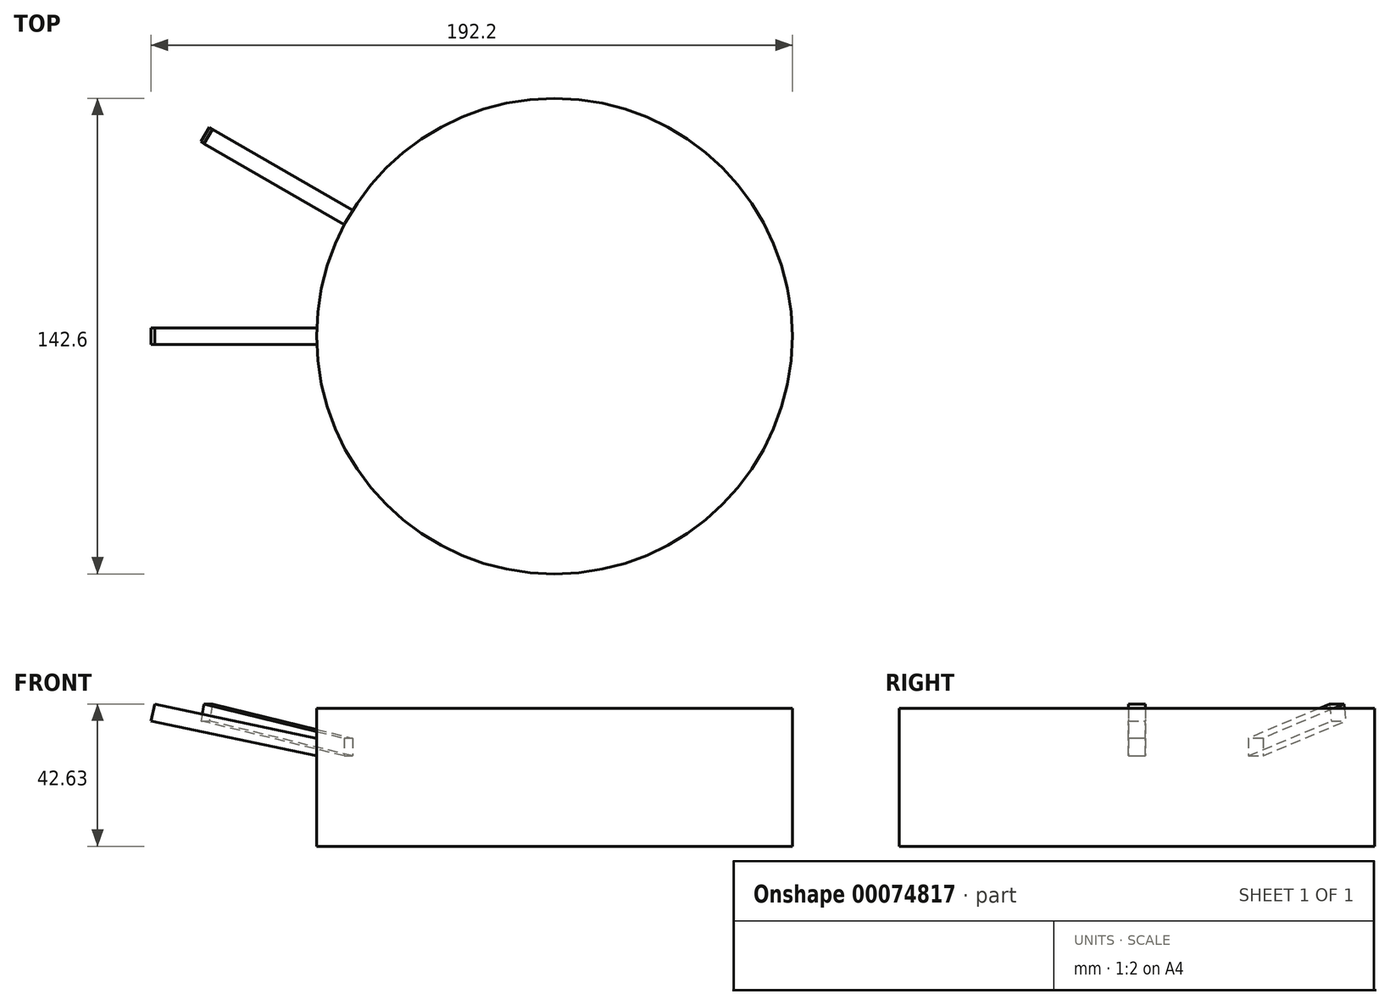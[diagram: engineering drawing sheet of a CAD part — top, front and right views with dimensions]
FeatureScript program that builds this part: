
annotation { "Feature Type Name" : "Feature", "Feature Type Description" : "" }
export const myFeature = defineFeature(function(context is Context, id is Id, definition is map)
    precondition{}
    {
        {
            var Q0;
            Q0=qCreatedBy(makeId("Front.planeOp"),FACE);
            var sketch = newSketch(context, id + "F0", { "sketchPlane" : qUnion([Q0])});
            skLineSegment(sketch, "E0.bottom", {"start": v(0, 0) * mm, "end": v(-71.3, 0) * mm});
            skLineSegment(sketch, "E0.top", {"start": v(0, 41.34) * mm, "end": v(-71.3, 41.34) * mm});
            skLineSegment(sketch, "E0.left", {"start": v(0, 0) * mm, "end": v(0, 41.34) * mm});
            skLineSegment(sketch, "E0.right", {"start": v(-71.3, 0) * mm, "end": v(-71.3, 41.34) * mm});
            skLineSegment(sketch, "E1", {"start": v(-119.83, 42.63) * mm, "end": v(-51.22, 28.15) * mm});
            skLineSegment(sketch, "E2", {"start": v(-51.22, 28.15) * mm, "end": v(-52.29, 23.09) * mm});
            skLineSegment(sketch, "E3", {"start": v(-52.29, 23.09) * mm, "end": v(-120.9, 37.57) * mm});
            skLineSegment(sketch, "E4", {"start": v(-119.83, 42.63) * mm, "end": v(-120.9, 37.57) * mm});
            skSolve(sketch);
        }
        {
            var Q0;
            {var subQ1=sQuery(id+"F0.wireOp",EDGE,"E0.bottom");Q0=makeQuery(id+"F0.imprint","IMPRINT",FACE,{"disambiguationData":[TD([[makeQuery(id+"F0.imprint","IMPRINT",EDGE,{"derivedFrom":subQ1}),-1.0]])]});}
            var Q1;
            {var subQ5=sQuery(id+"F0.wireOp",EDGE,"E2");Q1=makeQuery(id+"F0.imprint","IMPRINT",FACE,{"disambiguationData":[TD([[makeQuery(id+"F0.imprint","IMPRINT",EDGE,{"derivedFrom":subQ5}),-1.0]])]});}
            var Q2;
            Q2=sQuery(id+"F0.wireOp",EDGE,"E0.left");
            revolve(context, id + "F1", {"entities" : qUnion([Q0, Q1]), "axis" : qUnion([Q2]), "revolveType" : RevolveType.FULL});
        }
        {
            var Q0;
            {var subQ5=sQuery(id+"F0.wireOp",EDGE,"E4");Q0=makeQuery(id+"F0.imprint","IMPRINT",FACE,{"disambiguationData":[TD([[makeQuery(id+"F0.imprint","IMPRINT",EDGE,{"derivedFrom":subQ5}),1.0]])]});}
            var Q1;
            {var subQ5=sQuery(id+"F0.wireOp",EDGE,"E2");Q1=makeQuery(id+"F0.imprint","IMPRINT",FACE,{"disambiguationData":[TD([[makeQuery(id+"F0.imprint","IMPRINT",EDGE,{"derivedFrom":subQ5}),-1.0]])]});}
            extrude(context, id + "F2", {"entities" : qUnion([Q0, Q1]), "operationType" : NewBodyOperationType.ADD, "endBound" : BoundingType.SYMMETRIC, "depth" : 5 * mm});
        }
        {
            var Q0;
            Q0=makeQuery(id+"F2.opExtrude","SWEPT_FACE",FACE,{"disambiguationData":[OSD([sQuery(id+"F0.wireOp",EDGE,"E1")])]});
            var Q1;
            Q1=makeQuery(id+"F2.opExtrude","CAP_FACE",FACE,{"disambiguationData":[OSD([sQuery(id+"F0.wireOp",EDGE,"E1"),sQuery(id+"F0.wireOp",EDGE,"E2"),sQuery(id+"F0.wireOp",EDGE,"E3"),sQuery(id+"F0.wireOp",EDGE,"E4")])],"isStart":false});
            var Q2;
            Q2=makeQuery(id+"F2.opExtrude","SWEPT_FACE",FACE,{"disambiguationData":[OSD([sQuery(id+"F0.wireOp",EDGE,"E4")])]});
            var Q3;
            Q3=makeQuery(id+"F2.opExtrude","CAP_FACE",FACE,{"disambiguationData":[OSD([sQuery(id+"F0.wireOp",EDGE,"E1"),sQuery(id+"F0.wireOp",EDGE,"E2"),sQuery(id+"F0.wireOp",EDGE,"E3"),sQuery(id+"F0.wireOp",EDGE,"E4")])],"isStart":true});
            var Q4;
            Q4=makeQuery(id+"F2.opExtrude","SWEPT_FACE",FACE,{"disambiguationData":[OSD([sQuery(id+"F0.wireOp",EDGE,"E3")])]});
            var Q5;
            Q5=makeQuery(id+"F1.opRevolve","SWEPT_FACE",FACE,{"disambiguationData":[OSD([sQuery(id+"F0.wireOp",EDGE,"E0.right")])]});
            circularPattern(context, id + "F3", {"faces" : qUnion([Q0, Q1, Q2, Q3, Q4]), "axis" : qUnion([Q5]), "angle" : 30 * degree, "instanceCount" : 2, "patternType" : PatternType.FACE});
        }
    });
